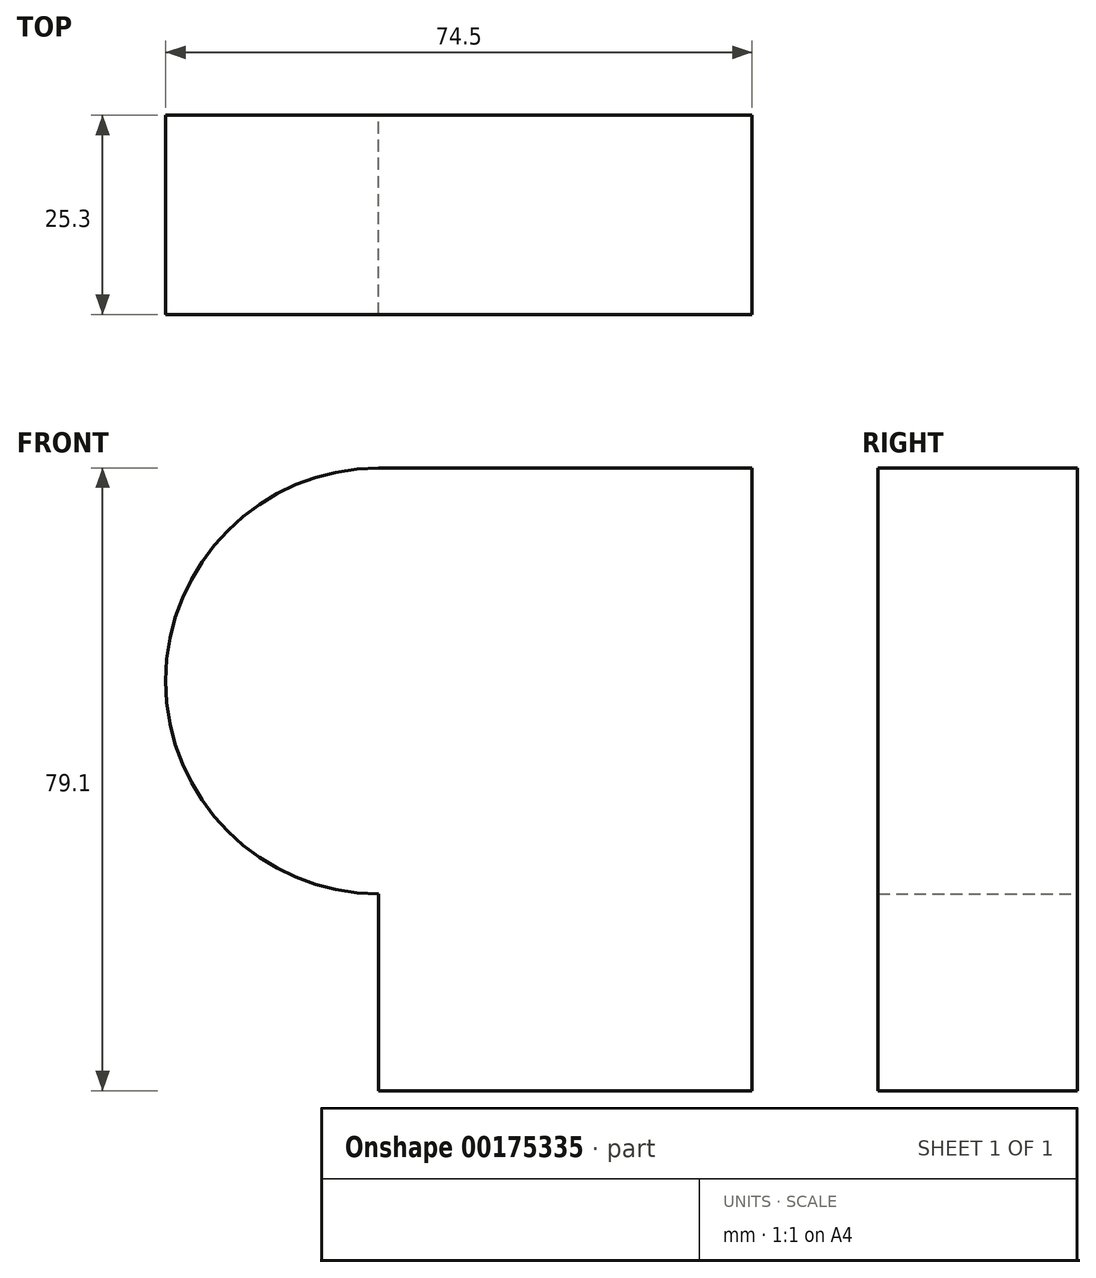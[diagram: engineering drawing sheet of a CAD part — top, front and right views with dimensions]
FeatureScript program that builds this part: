
annotation { "Feature Type Name" : "Feature", "Feature Type Description" : "" }
export const myFeature = defineFeature(function(context is Context, id is Id, definition is map)
    precondition{}
    {
        {
            var Q0;
            Q0=qCreatedBy(makeId("Front.planeOp"),FACE);
            var sketch = newSketch(context, id + "F0", { "sketchPlane" : qUnion([Q0])});
            skLineSegment(sketch, "E0.bottom", {"start": v(-47.45, -22.66) * mm, "end": v(59.06, -22.66) * mm});
            skLineSegment(sketch, "E0.top", {"start": v(-47.45, 31.44) * mm, "end": v(59.06, 31.44) * mm});
            skArc(sketch, "E1", {"start": v(-47.45, 31.44) * mm, "mid": v(-74.5, 4.4) * mm, "end": v(-47.45, -22.66) * mm});
            skArc(sketch, "E2", {"start": v(59.06, -22.66) * mm, "mid": v(86.12, 4.4) * mm, "end": v(59.06, 31.44) * mm});
            skLineSegment(sketch, "E3", {"start": v(5.8, 31.44) * mm, "end": v(5.8, -22.66) * mm});
            skLineSegment(sketch, "E4", {"start": v(0, 31.44) * mm, "end": v(0, -22.66) * mm});
            skSolve(sketch);
        }
        {
            var Q0;
            {var subQ0=sQuery(id+"F0.wireOp",EDGE,"E1");Q0=makeQuery(id+"F0.imprint","IMPRINT",FACE,{"disambiguationData":[TD([[makeQuery(id+"F0.imprint","IMPRINT",EDGE,{"derivedFrom":subQ0}),1.0]])]});}
            extrude(context, id + "F1", {"entities" : qUnion([Q0]), "depth" : 25.3 * mm});
        }
        {
            var Q0;
            Q0=makeQuery(id+"F1.opExtrude","SWEPT_FACE",FACE,{"disambiguationData":[OSD([sQuery(id+"F0.wireOp",EDGE,"E0.bottom")])]});
            var Q1;
            Q1=makeQuery(id+"F1.opExtrude","SWEPT_FACE",FACE,{"disambiguationData":[OSD([sQuery(id+"F0.wireOp",EDGE,"E0.top")])]});
            extrude(context, id + "F2", {"entities" : qUnion([Q0, Q1]), "operationType" : NewBodyOperationType.ADD, "depth" : 25 * mm});
        }
    });
